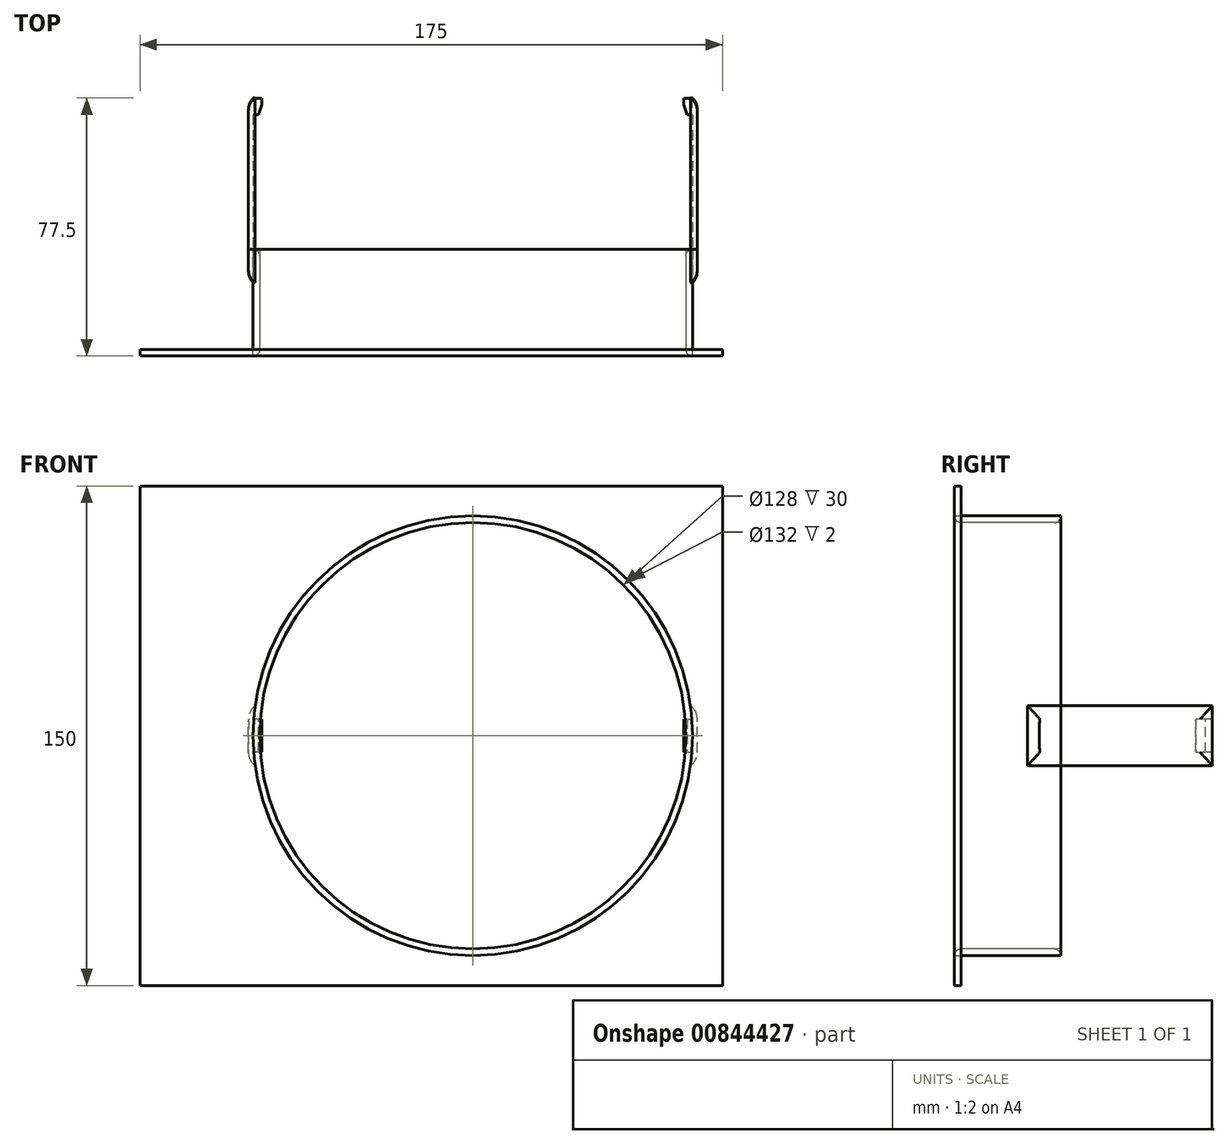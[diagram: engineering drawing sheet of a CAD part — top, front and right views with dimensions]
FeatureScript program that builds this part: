
annotation { "Feature Type Name" : "Feature", "Feature Type Description" : "" }
export const myFeature = defineFeature(function(context is Context, id is Id, definition is map)
    precondition{}
    {
        {
            var Q0;
            Q0=qCreatedBy(makeId("Front.planeOp"),FACE);
            var sketch = newSketch(context, id + "F0", { "sketchPlane" : qUnion([Q0])});
            skLineSegment(sketch, "E0.bottom", {"start": v(-100, 75) * mm, "end": v(75, 75) * mm});
            skLineSegment(sketch, "E0.top", {"start": v(-100, -75) * mm, "end": v(75, -75) * mm});
            skLineSegment(sketch, "E0.left", {"start": v(-100, 75) * mm, "end": v(-100, -75) * mm});
            skLineSegment(sketch, "E0.right", {"start": v(75, 75) * mm, "end": v(75, -75) * mm});
            skCircle(sketch, "E1", {"center": v(0, 0) * mm, "radius": 64 * mm});
            skCircle(sketch, "E2", {"center": v(0, 0) * mm, "radius": 66 * mm});
            skSolve(sketch);
        }
        {
            var Q0;
            Q0 = qSketchRegion(id + "F0", true);
            extrude(context, id + "F1", {"entities" : qUnion([Q0]), "depth" : 2 * mm, "offsetDistance" : 25 * mm});
        }
        {
            var Q0;
            Q0=makeQuery(id+"F1.opExtrude","CAP_FACE",FACE,{"disambiguationData":[OSD([sQuery(id+"F0.wireOp",EDGE,"E0.bottom"),sQuery(id+"F0.wireOp",EDGE,"E0.top"),sQuery(id+"F0.wireOp",EDGE,"E0.left"),sQuery(id+"F0.wireOp",EDGE,"E0.right"),sQuery(id+"F0.wireOp",EDGE,"E2")])],"isStart":true});
            var sketch = newSketch(context, id + "F2", { "sketchPlane" : qUnion([Q0])});
            skCircle(sketch, "E3", {"center": v(0, 0) * mm, "radius": 64 * mm});
            skCircle(sketch, "E4", {"center": v(0, 0) * mm, "radius": 66 * mm});
            skSolve(sketch);
        }
        {
            var Q0;
            Q0 = qSketchRegion(id + "F2", true);
            var Q1;
            Q1=makeQuery(id+"F0.imprint","IMPRINT",FACE,{"disambiguationData":[TD([[makeQuery(id+"F0.imprint","IMPRINT",EDGE,{"derivedFrom":sQuery(id+"F0.wireOp",EDGE,"E1")}),-1.0]])]});
            extrude(context, id + "F3", {"entities" : qUnion([Q0, Q1]), "depth" : 30 * mm, "offsetDistance" : 25 * mm});
        }
        {
            var Q0;
            Q0=makeQuery(id+"F3.opExtrude","CAP_FACE",FACE,{"disambiguationData":[OSD([sQuery(id+"F0.wireOp",EDGE,"E1"),sQuery(id+"F0.wireOp",EDGE,"E2")])],"isStart":false});
            var sketch = newSketch(context, id + "F4", { "sketchPlane" : qUnion([Q0])});
            skLineSegment(sketch, "E5.bottom", {"start": v(-65.38, -9) * mm, "end": v(-67.4, -9) * mm});
            skLineSegment(sketch, "E5.top", {"start": v(-65.38, 9) * mm, "end": v(-67.38, 9) * mm});
            skLineSegment(sketch, "E5.right", {"start": v(-67.4, -9) * mm, "end": v(-67.38, 9) * mm});
            skArc(sketch, "E6", {"start": v(-65.38, 9) * mm, "mid": v(-66, 0) * mm, "end": v(-65.38, -9) * mm});
            skSolve(sketch);
        }
        {
            var Q0;
            {var subQ0=sQuery(id+"F4.wireOp",EDGE,"E6");var subQ1=sQuery(id+"F4.wireOp",EDGE,"E5.top");var subQ2=makeQuery(id+"F4.imprint","INTERSECT",VERTEX,{"derivedFrom":[subQ1,subQ0]});Q0=makeQuery(id+"F4.imprint","IMPRINT",FACE,{"disambiguationData":[TD([[makeQuery(id+"F4.imprint","IMPRINT",EDGE,{"disambiguationData":[TD([[subQ2,-1.0]])],"derivedFrom":subQ1}),1.0]])]});}
            var Q1;
            {var subQ5=sQuery(id+"F4.wireOp",EDGE,"E5.bottom");Q1=makeQuery(id+"F4.imprint","IMPRINT",FACE,{"disambiguationData":[TD([[makeQuery(id+"F4.imprint","IMPRINT",EDGE,{"derivedFrom":subQ5}),-1.0]])]});}
            extrude(context, id + "F5", {"entities" : qUnion([Q0, Q1]), "depth" : 45.5 * mm, "offsetDistance" : 25 * mm});
        }
        {
            var Q0;
            Q0 = qSketchRegion(id + "F4", true);
            extrude(context, id + "F6", {"entities" : qUnion([Q0]), "depth" : -10 * mm, "offsetDistance" : 25 * mm});
        }
        {
            var Q0;
            Q0=makeQuery(id+"F6.opExtrude","CAP_EDGE",EDGE,{"disambiguationData":[OSD([sQuery(id+"F4.wireOp",EDGE,"E5.right")])],"isStart":false});
            fillet(context, id + "F7", {"entities" : qUnion([Q0]), "radius" : 5 * mm, "tangentPropagation" : true, "allowEdgeOverflow" : false});
        }
        {
            var Q0;
            Q0=makeQuery(id+"F5.opExtrude","CAP_EDGE",EDGE,{"disambiguationData":[OSD([sQuery(id+"F4.wireOp",EDGE,"E5.right")])],"isStart":false});
            fillet(context, id + "F8", {"entities" : qUnion([Q0]), "radius" : 5 * mm, "tangentPropagation" : true, "allowEdgeOverflow" : false});
        }
        {
            var Q0;
            Q0=makeQuery(id+"F5.opExtrude","SWEPT_EDGE",EDGE,{"disambiguationData":[OSD([sQuery(id+"F4.wireOp",EDGE,"E5.bottom"),sQuery(id+"F4.wireOp",EDGE,"E5.right")])]});
            var Q1;
            Q1=makeQuery(id+"F5.opExtrude","SWEPT_EDGE",EDGE,{"disambiguationData":[OSD([sQuery(id+"F4.wireOp",EDGE,"E5.top"),sQuery(id+"F4.wireOp",EDGE,"E5.right")])]});
            var Q2;
            Q2=makeQuery(id+"F6.opExtrude","SWEPT_EDGE",EDGE,{"disambiguationData":[OSD([sQuery(id+"F4.wireOp",EDGE,"E5.bottom"),sQuery(id+"F4.wireOp",EDGE,"E5.right")])]});
            var Q3;
            Q3=makeQuery(id+"F6.opExtrude","SWEPT_EDGE",EDGE,{"disambiguationData":[OSD([sQuery(id+"F4.wireOp",EDGE,"E5.top"),sQuery(id+"F4.wireOp",EDGE,"E5.right")])]});
            fillet(context, id + "F9", {"entities" : qUnion([Q0, Q1, Q2, Q3]), "radius" : 5 * mm, "tangentPropagation" : true, "allowEdgeOverflow" : false});
        }
        {
            var Q0;
            Q0=makeQuery(id+"F5.opExtrude","SWEPT_FACE",FACE,{"disambiguationData":[OSD([sQuery(id+"F4.wireOp",EDGE,"E5.right")])]});
            var sketch = newSketch(context, id + "F10", { "sketchPlane" : qUnion([Q0])});
            skLineSegment(sketch, "E7.bottom", {"start": v(75.45, 4.9) * mm, "end": v(70.45, 4.9) * mm});
            skLineSegment(sketch, "E7.top", {"start": v(75.45, -5.08) * mm, "end": v(70.45, -5.08) * mm});
            skLineSegment(sketch, "E7.left", {"start": v(75.45, 4.9) * mm, "end": v(75.45, -5.08) * mm});
            skLineSegment(sketch, "E7.right", {"start": v(70.45, 4.9) * mm, "end": v(70.45, -5.08) * mm});
            skSolve(sketch);
        }
        {
            var Q0;
            Q0 = qSketchRegion(id + "F10", true);
            extrude(context, id + "F11", {"entities" : qUnion([Q0]), "operationType" : NewBodyOperationType.ADD, "depth" : -4 * mm, "offsetDistance" : 25 * mm});
        }
        {
            var Q0;
            Q0=makeQuery(id+"F6.opExtrude","SWEPT_BODY",BODY,{"disambiguationData":[OSD([sQuery(id+"F4.wireOp",EDGE,"E5.bottom"),sQuery(id+"F4.wireOp",EDGE,"E5.top"),sQuery(id+"F4.wireOp",EDGE,"E5.right"),sQuery(id+"F4.wireOp",EDGE,"E6")])]});
            var Q1;
            Q1=makeQuery(id+"F5.opExtrude","SWEPT_BODY",BODY,{"disambiguationData":[OSD([sQuery(id+"F4.wireOp",EDGE,"E5.bottom"),sQuery(id+"F4.wireOp",EDGE,"E5.top"),sQuery(id+"F4.wireOp",EDGE,"E5.right"),sQuery(id+"F4.wireOp",EDGE,"E6")])]});
            var Q2;
            Q2=qCreatedBy(makeId("Right.planeOp"),FACE);
            mirror(context, id + "F12", {"entities" : qUnion([Q0, Q1]), "mirrorPlane" : qUnion([Q2])});
        }
        {
            var Q0;
            Q0=makeQuery(id+"F11.opExtrude","CAP_EDGE",EDGE,{"disambiguationData":[OSD([sQuery(id+"F10.wireOp",EDGE,"E7.left")])],"isStart":true});
            fillet(context, id + "F13", {"entities" : qUnion([Q0]), "radius" : 5 * mm, "tangentPropagation" : true, "allowEdgeOverflow" : false});
        }
        {
            var Q0;
            Q0=makeQuery(id+"F11.opExtrude","CAP_EDGE",EDGE,{"disambiguationData":[OSD([sQuery(id+"F10.wireOp",EDGE,"E7.right")])],"isStart":false});
            chamfer(context, id + "F14", {"entities" : qUnion([Q0]), "chamferType" : ChamferType.TWO_OFFSETS, "width1" : 1 * mm, "oppositeDirection" : false, "width2" : 3 * mm, "tangentPropagation" : true});
        }
        {
            var Q0;
            Q0=makeQuery(id+"F12.opPattern","COPY",EDGE,{"derivedFrom":makeQuery(id+"F11.opExtrude","CAP_EDGE",EDGE,{"disambiguationData":[OSD([sQuery(id+"F10.wireOp",EDGE,"E7.right")])],"isStart":false}),"instanceName":"1"});
            chamfer(context, id + "F15", {"entities" : qUnion([Q0]), "chamferType" : ChamferType.TWO_OFFSETS, "width1" : 3 * mm, "oppositeDirection" : false, "width2" : 1 * mm, "tangentPropagation" : true});
        }
        {
            var Q0;
            Q0=makeQuery(id+"F12.opPattern","COPY",EDGE,{"derivedFrom":makeQuery(id+"F11.opExtrude","CAP_EDGE",EDGE,{"disambiguationData":[OSD([sQuery(id+"F10.wireOp",EDGE,"E7.left")])],"isStart":true}),"instanceName":"1"});
            fillet(context, id + "F16", {"entities" : qUnion([Q0]), "radius" : 5 * mm, "tangentPropagation" : true, "allowEdgeOverflow" : false});
        }
        {
            var Q0;
            Q0=makeQuery(id+"F3.opExtrude","CAP_FACE",FACE,{"disambiguationData":[OSD([sQuery(id+"F0.wireOp",EDGE,"E1"),sQuery(id+"F0.wireOp",EDGE,"E2")])],"isStart":true});
            extrude(context, id + "F17", {"entities" : qUnion([Q0]), "depth" : 2 * mm, "offsetDistance" : 25 * mm});
        }
        {
            var Q0;
            Q0=makeQuery(id+"F17.opExtrude","CAP_EDGE",EDGE,{"disambiguationData":[OSD([sQuery(id+"F0.wireOp",EDGE,"E1")])],"isStart":false});
            fillet(context, id + "F18", {"entities" : qUnion([Q0]), "radius" : 2 * mm, "tangentPropagation" : true, "allowEdgeOverflow" : false});
        }
        {
            var Q0;
            Q0=makeQuery(id+"F3.opExtrude","CAP_EDGE",EDGE,{"disambiguationData":[OSD([sQuery(id+"F0.wireOp",EDGE,"E1")])],"isStart":false});
            fillet(context, id + "F19", {"entities" : qUnion([Q0]), "radius" : 2 * mm, "tangentPropagation" : true, "allowEdgeOverflow" : false});
        }
    });
